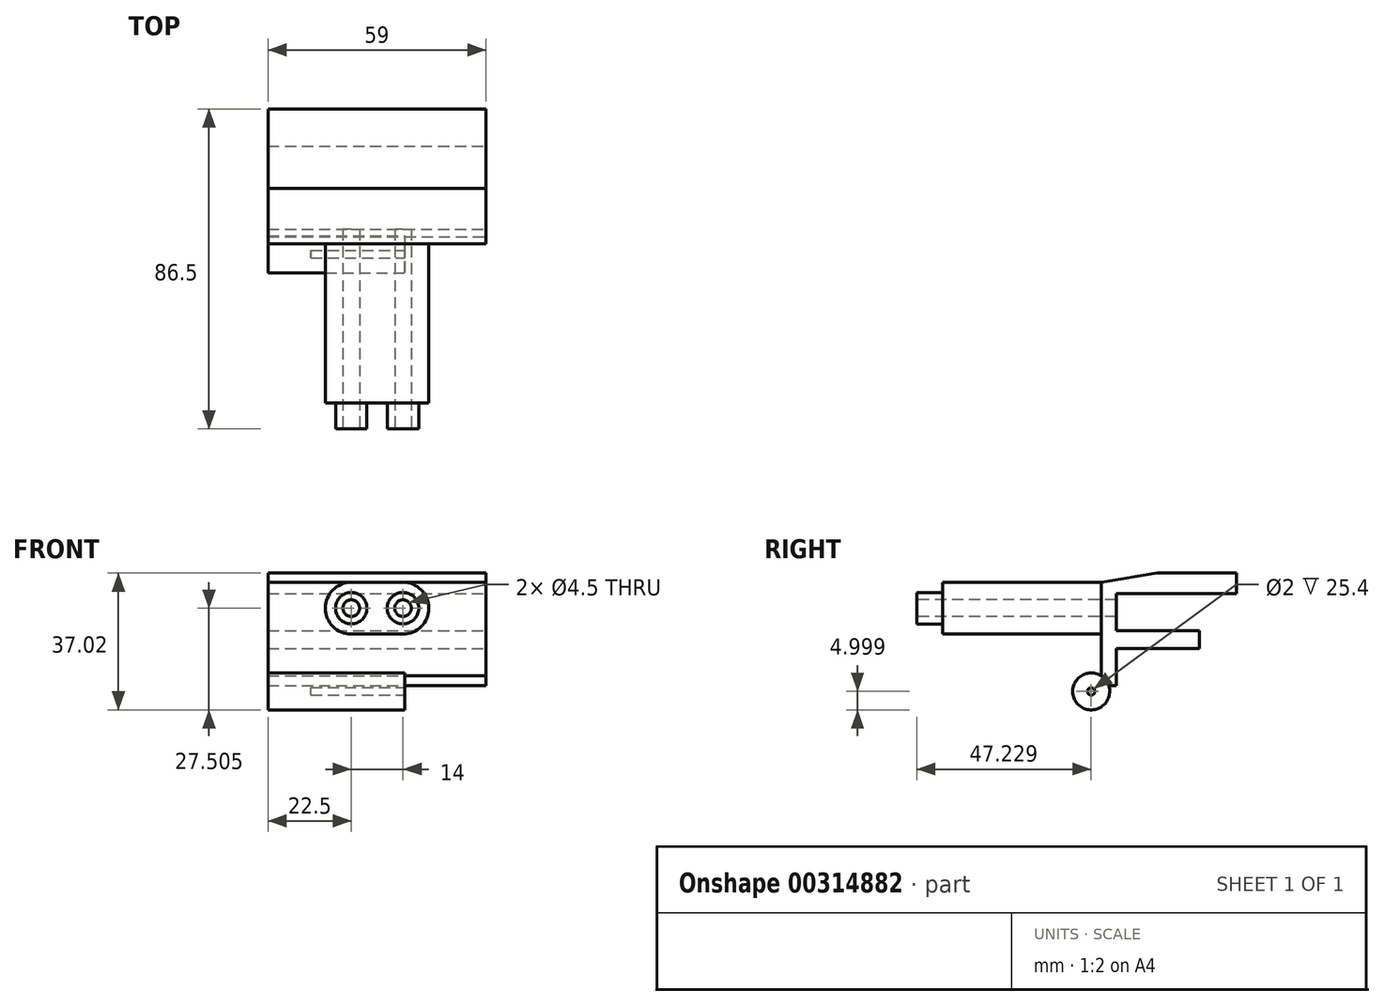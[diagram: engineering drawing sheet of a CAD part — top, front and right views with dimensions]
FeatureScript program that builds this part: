
annotation { "Feature Type Name" : "Feature", "Feature Type Description" : "" }
export const myFeature = defineFeature(function(context is Context, id is Id, definition is map)
    precondition{}
    {
        {
            var Q0;
            Q0=qCreatedBy(makeId("Right.planeOp"),FACE);
            var sketch = newSketch(context, id + "F0", { "sketchPlane" : qUnion([Q0])});
            skLineSegment(sketch, "E0.bottom", {"start": v(-27.18, 24.44) * mm, "end": v(67.82, 24.44) * mm});
            skLineSegment(sketch, "E0.top", {"start": v(-27.18, -25.56) * mm, "end": v(67.82, -25.56) * mm});
            skLineSegment(sketch, "E0.left", {"start": v(-27.18, 24.44) * mm, "end": v(-27.18, -25.56) * mm});
            skLineSegment(sketch, "E0.right", {"start": v(67.82, 24.44) * mm, "end": v(67.82, -25.56) * mm});
            skSolve(sketch);
        }
        {
            var Q0;
            Q0=makeQuery(id+"F0.imprint","IMPRINT",FACE,{"disambiguationData":[TD([[makeQuery(id+"F0.imprint","IMPRINT",EDGE,{"derivedFrom":sQuery(id+"F0.wireOp",EDGE,"E0.bottom")}),-1.0]])]});
            extrude(context, id + "F1", {"entities" : qUnion([Q0]), "endBound" : BoundingType.SYMMETRIC, "depth" : 59 * mm});
        }
        {
            var Q0;
            Q0=makeQuery(id+"F1.opExtrude","CAP_FACE",FACE,{"disambiguationData":[OSD([sQuery(id+"F0.wireOp",EDGE,"E0.bottom"),sQuery(id+"F0.wireOp",EDGE,"E0.top"),sQuery(id+"F0.wireOp",EDGE,"E0.left"),sQuery(id+"F0.wireOp",EDGE,"E0.right")])],"isStart":false});
            var sketch = newSketch(context, id + "F2", { "sketchPlane" : qUnion([Q0])});
            skLineSegment(sketch, "E1", {"start": v(-21.45, 24.44) * mm, "end": v(-21.45, 18.29) * mm});
            skLineSegment(sketch, "E2", {"start": v(-21.45, 18.29) * mm, "end": v(-13.49, 18.29) * mm});
            skLineSegment(sketch, "E3", {"start": v(-13.49, 18.29) * mm, "end": v(-21.45, 24.44) * mm});
            skLineSegment(sketch, "E4", {"start": v(-21.45, 18.29) * mm, "end": v(-27.18, 18.29) * mm});
            skLineSegment(sketch, "E5", {"start": v(-27.18, 18.29) * mm, "end": v(-27.18, 4.29) * mm});
            skLineSegment(sketch, "E6", {"start": v(-27.18, 4.29) * mm, "end": v(22.82, 4.29) * mm});
            skLineSegment(sketch, "E7", {"start": v(-27.18, 11.29) * mm, "end": v(26.82, 11.29) * mm});
            skLineSegment(sketch, "E8", {"start": v(-13.49, 18.29) * mm, "end": v(22.82, 18.29) * mm});
            skPoint(sketch, "E9.endSnap0", {"position": v(21.6, 18.29) * mm});
            skLineSegment(sketch, "E10", {"start": v(22.82, 18.29) * mm, "end": v(37.83, 20.8) * mm});
            skLineSegment(sketch, "E11", {"start": v(22.82, 4.29) * mm, "end": v(22.82, -9.71) * mm});
            skLineSegment(sketch, "E12", {"start": v(22.82, -9.71) * mm, "end": v(26.82, -9.71) * mm});
            skLineSegment(sketch, "E13", {"start": v(26.82, -9.71) * mm, "end": v(26.82, 15.29) * mm});
            skArc(sketch, "E14", {"start": v(22.82, -7.06) * mm, "mid": v(16.05, -14.23) * mm, "end": v(24.82, -9.71) * mm});
            skPoint(sketch, "E15.end.orphan", {"position": v(34.19, -8.71) * mm});
            skLineSegment(sketch, "E16", {"start": v(26.82, 5.19) * mm, "end": v(49.32, 5.19) * mm});
            skLineSegment(sketch, "E17", {"start": v(49.32, 5.19) * mm, "end": v(49.32, 0.39) * mm});
            skLineSegment(sketch, "E18", {"start": v(49.32, 0.39) * mm, "end": v(26.82, 0.39) * mm});
            skLineSegment(sketch, "E19", {"start": v(26.82, 15.29) * mm, "end": v(59.32, 15.29) * mm});
            skLineSegment(sketch, "E20", {"start": v(37.83, 20.8) * mm, "end": v(59.32, 20.8) * mm});
            skLineSegment(sketch, "E21", {"start": v(59.32, 20.8) * mm, "end": v(59.32, 15.29) * mm});
            skSolve(sketch);
        }
        {
            var Q0;
            {var subQ0=sQuery(id+"F2.wireOp",EDGE,"E1");Q0=makeQuery(id+"F2.imprint","IMPRINT",FACE,{"disambiguationData":[TD([[makeQuery(id+"F2.imprint","IMPRINT",EDGE,{"derivedFrom":subQ0}),-1.0]])]});}
            var Q1;
            {var subQ9=sQuery(id+"F2.wireOp",EDGE,"E3");Q1=makeQuery(id+"F2.imprint","IMPRINT",FACE,{"disambiguationData":[TD([[makeQuery(id+"F2.imprint","IMPRINT",EDGE,{"derivedFrom":subQ9}),-1.0]])]});}
            extrude(context, id + "F3", {"entities" : qUnion([Q0, Q1]), "operationType" : NewBodyOperationType.REMOVE, "endBound" : BoundingType.THROUGH_ALL, "oppositeDirection" : true, "depth" : 25.4 * mm});
        }
        {
            var Q0;
            Q0=makeQuery(id+"F1.opExtrude","CAP_FACE",FACE,{"disambiguationData":[OSD([sQuery(id+"F0.wireOp",EDGE,"E0.bottom"),sQuery(id+"F0.wireOp",EDGE,"E0.top"),sQuery(id+"F0.wireOp",EDGE,"E0.left"),sQuery(id+"F0.wireOp",EDGE,"E0.right")])],"isStart":false});
            var sketch = newSketch(context, id + "F4", { "sketchPlane" : qUnion([Q0])});
            skCircle(sketch, "E22", {"center": v(20.05, -11.22) * mm, "radius": 5 * mm});
            skSolve(sketch);
        }
        {
            var Q0;
            Q0 = qSketchRegion(id + "F4", true);
            extrude(context, id + "F5", {"entities" : qUnion([Q0]), "operationType" : NewBodyOperationType.REMOVE, "oppositeDirection" : true, "depth" : 22 * mm});
        }
        {
            var Q0;
            Q0=makeQuery(id+"F5.boolean.opBoolean","COPY",FACE,{"derivedFrom":makeQuery(id+"F5.opExtrude","CAP_FACE",FACE,{"disambiguationData":[OSD([sQuery(id+"F4.wireOp",EDGE,"E22")])],"isStart":false})});
            var sketch = newSketch(context, id + "F6", { "sketchPlane" : qUnion([Q0])});
            skCircle(sketch, "E23", {"center": v(20.05, -11.22) * mm, "radius": 1 * mm});
            skSolve(sketch);
        }
        {
            var Q0;
            Q0=makeQuery(id+"F6.imprint","IMPRINT",FACE,{"disambiguationData":[TD([[makeQuery(id+"F6.imprint","IMPRINT",EDGE,{"derivedFrom":sQuery(id+"F6.wireOp",EDGE,"E23")}),1.0]])]});
            extrude(context, id + "F7", {"entities" : qUnion([Q0]), "operationType" : NewBodyOperationType.REMOVE, "oppositeDirection" : true, "depth" : 25.4 * mm});
        }
        {
            var Q0;
            Q0=makeQuery(id+"F1.opExtrude","SWEPT_FACE",FACE,{"disambiguationData":[OSD([sQuery(id+"F0.wireOp",EDGE,"E0.left")])]});
            var sketch = newSketch(context, id + "F8", { "sketchPlane" : qUnion([Q0])});
            skArc(sketch, "E24", {"start": v(-7, 18.29) * mm, "mid": v(-14, 11.29) * mm, "end": v(-7, 4.29) * mm});
            skPoint(sketch, "E24.centerSnap0", {"position": v(-29.5, 11.29) * mm});
            skArc(sketch, "E25", {"start": v(7, 4.29) * mm, "mid": v(14, 11.29) * mm, "end": v(7, 18.29) * mm});
            skPoint(sketch, "E25.centerSnap0", {"position": v(29.5, 11.29) * mm});
            skCircle(sketch, "E26", {"center": v(-7, 11.29) * mm, "radius": 2.25 * mm});
            skCircle(sketch, "E27", {"center": v(7, 11.29) * mm, "radius": 2.25 * mm});
            skLineSegment(sketch, "E28", {"start": v(-7, 18.29) * mm, "end": v(7, 18.29) * mm});
            skLineSegment(sketch, "E29", {"start": v(-7, 4.29) * mm, "end": v(7, 4.29) * mm});
            skPoint(sketch, "E30.end.orphan", {"position": v(0, 4.29) * mm});
            skPoint(sketch, "E30.start.orphan", {"position": v(0, 18.29) * mm});
            skSolve(sketch);
        }
        {
            var Q0;
            {var subQ0=sQuery(id+"F8.wireOp",EDGE,"E25");Q0=makeQuery(id+"F8.imprint","IMPRINT",FACE,{"disambiguationData":[TD([[makeQuery(id+"F8.imprint","IMPRINT",EDGE,{"derivedFrom":subQ0}),-1.0]])]});}
            var Q1;
            {var subQ0=sQuery(id+"F8.wireOp",EDGE,"E24");Q1=makeQuery(id+"F8.imprint","IMPRINT",FACE,{"disambiguationData":[TD([[makeQuery(id+"F8.imprint","IMPRINT",EDGE,{"derivedFrom":subQ0}),-1.0]])]});}
            var Q2;
            Q2=makeQuery(id+"F8.imprint","IMPRINT",FACE,{"disambiguationData":[TD([[makeQuery(id+"F8.imprint","IMPRINT",EDGE,{"derivedFrom":sQuery(id+"F8.wireOp",EDGE,"E26")}),1.0]])]});
            var Q3;
            Q3=makeQuery(id+"F8.imprint","IMPRINT",FACE,{"disambiguationData":[TD([[makeQuery(id+"F8.imprint","IMPRINT",EDGE,{"derivedFrom":sQuery(id+"F8.wireOp",EDGE,"E27")}),1.0]])]});
            extrude(context, id + "F9", {"entities" : qUnion([Q0, Q1, Q2, Q3]), "operationType" : NewBodyOperationType.REMOVE, "oppositeDirection" : true, "depth" : 50 * mm});
        }
        {
            var Q0;
            Q0=makeQuery(id+"F9.boolean.opBoolean","COPY",FACE,{"derivedFrom":makeQuery(id+"F9.opExtrude","CAP_FACE",FACE,{"disambiguationData":[OSD([sQuery(id+"F8.wireOp",EDGE,"E26")])],"isStart":false})});
            var Q1;
            Q1=makeQuery(id+"F9.boolean.opBoolean","COPY",FACE,{"derivedFrom":makeQuery(id+"F9.opExtrude","CAP_FACE",FACE,{"disambiguationData":[OSD([sQuery(id+"F8.wireOp",EDGE,"E27")])],"isStart":false})});
            extrude(context, id + "F10", {"entities" : qUnion([Q0, Q1]), "operationType" : NewBodyOperationType.REMOVE, "endBound" : BoundingType.THROUGH_ALL, "oppositeDirection" : true, "depth" : 25 * mm});
        }
        {
            var Q0;
            Q0=makeQuery(id+"F3.boolean.opBoolean","COPY",FACE,{"derivedFrom":makeQuery(id+"F3.opExtrude","SWEPT_FACE",FACE,{"disambiguationData":[OSD([sQuery(id+"F2.wireOp",EDGE,"E1")])]})});
            var sketch = newSketch(context, id + "F11", { "sketchPlane" : qUnion([Q0])});
            skLineSegment(sketch, "E31", {"start": v(-7, 18.29) * mm, "end": v(-7, 24.44) * mm});
            skLineSegment(sketch, "E32", {"start": v(7, 18.29) * mm, "end": v(7, 24.44) * mm});
            skSolve(sketch);
        }
        {
            var Q0;
            Q0 = qSketchRegion(id + "F11", true);
            var Q1;
            {var subQ0=sQuery(id+"F11.wireOp",EDGE,"E31");Q1=makeQuery(id+"F11.imprint","IMPRINT",FACE,{"disambiguationData":[TD([[makeQuery(id+"F11.imprint","IMPRINT",EDGE,{"derivedFrom":subQ0}),1.0]])]});}
            var Q2;
            {var subQ0=sQuery(id+"F11.wireOp",EDGE,"E32");Q2=makeQuery(id+"F11.imprint","IMPRINT",FACE,{"disambiguationData":[TD([[makeQuery(id+"F11.imprint","IMPRINT",EDGE,{"derivedFrom":subQ0}),-1.0]])]});}
            extrude(context, id + "F12", {"entities" : qUnion([Q0, Q1, Q2]), "operationType" : NewBodyOperationType.REMOVE, "oppositeDirection" : true, "depth" : 25 * mm});
        }
        {
            var Q0;
            Q0=makeQuery(id+"F12.boolean.opBoolean","COPY",FACE,{"derivedFrom":makeQuery(id+"F12.opExtrude","SWEPT_FACE",FACE,{"disambiguationData":[OSD([sQuery(id+"F11.wireOp",EDGE,"E31")])]})});
            extrude(context, id + "F13", {"entities" : qUnion([Q0]), "operationType" : NewBodyOperationType.REMOVE, "oppositeDirection" : true, "depth" : 5 * mm});
        }
        {
            var Q0;
            Q0=makeQuery(id+"F12.boolean.opBoolean","COPY",FACE,{"derivedFrom":makeQuery(id+"F12.opExtrude","SWEPT_FACE",FACE,{"disambiguationData":[OSD([sQuery(id+"F11.wireOp",EDGE,"E32")])]})});
            extrude(context, id + "F14", {"entities" : qUnion([Q0]), "operationType" : NewBodyOperationType.REMOVE, "oppositeDirection" : true, "depth" : 5 * mm});
        }
        {
            var Q0;
            Q0=makeQuery(id+"F13.boolean.opBoolean","COPY",FACE,{"derivedFrom":makeQuery(id+"F13.opExtrude","CAP_FACE",FACE,{"disambiguationData":[OSD([sQuery(id+"F11.wireOp",EDGE,"E31")])],"isStart":false})});
            var sketch = newSketch(context, id + "F15", { "sketchPlane" : qUnion([Q0])});
            skFitSpline(sketch, "E33", {"points": [v(21.45, 24.44) * mm, v(19.48, 20.4) * mm, v(13.49, 18.29) * mm], "startDerivative": vector(0, -5.6) * mm, "endDerivative": vector(-11.26, 0) * mm});
            skSolve(sketch);
        }
        {
            var Q0;
            Q0=makeQuery(id+"F15.imprint","IMPRINT",FACE,{"disambiguationData":[TD([[makeQuery(id+"F15.imprint","IMPRINT",EDGE,{"derivedFrom":sQuery(id+"F15.wireOp",EDGE,"E33")}),-1.0]])]});
            extrude(context, id + "F16", {"entities" : qUnion([Q0]), "operationType" : NewBodyOperationType.REMOVE, "oppositeDirection" : true, "depth" : 25 * mm});
        }
        {
            var Q0;
            Q0=makeQuery(id+"F3.boolean.opBoolean","COPY",FACE,{"derivedFrom":makeQuery(id+"F3.opExtrude","SWEPT_FACE",FACE,{"disambiguationData":[OSD([sQuery(id+"F2.wireOp",EDGE,"E1")])]})});
            var sketch = newSketch(context, id + "F17", { "sketchPlane" : qUnion([Q0])});
            skLineSegment(sketch, "E34.bottom", {"start": v(-0.5, 24.44) * mm, "end": v(0.5, 24.44) * mm});
            skLineSegment(sketch, "E34.top", {"start": v(-0.5, 20.04) * mm, "end": v(0.5, 20.04) * mm});
            skLineSegment(sketch, "E34.left", {"start": v(0.5, 24.44) * mm, "end": v(0.5, 20.04) * mm});
            skLineSegment(sketch, "E34.right", {"start": v(-0.5, 24.44) * mm, "end": v(-0.5, 20.04) * mm});
            skLineSegment(sketch, "E35.bottom", {"start": v(-0.5, 20.04) * mm, "end": v(-2, 20.04) * mm});
            skLineSegment(sketch, "E35.top", {"start": v(-0.5, 24.44) * mm, "end": v(-2, 24.44) * mm});
            skLineSegment(sketch, "E35.left", {"start": v(-0.5, 20.04) * mm, "end": v(-0.5, 24.44) * mm});
            skLineSegment(sketch, "E35.right", {"start": v(-2, 20.04) * mm, "end": v(-2, 24.44) * mm});
            skLineSegment(sketch, "E36.bottom", {"start": v(0.5, 20.04) * mm, "end": v(2, 20.04) * mm});
            skLineSegment(sketch, "E36.top", {"start": v(0.5, 24.44) * mm, "end": v(2, 24.44) * mm});
            skLineSegment(sketch, "E36.left", {"start": v(0.5, 20.04) * mm, "end": v(0.5, 24.44) * mm});
            skLineSegment(sketch, "E36.right", {"start": v(2, 20.04) * mm, "end": v(2, 24.44) * mm});
            skSolve(sketch);
        }
        {
            var Q0;
            Q0=makeQuery(id+"F17.imprint","IMPRINT",FACE,{"disambiguationData":[TD([[makeQuery(id+"F17.imprint","IMPRINT",EDGE,{"derivedFrom":sQuery(id+"F17.wireOp",EDGE,"E35.bottom")}),-1.0]])]});
            var Q1;
            Q1=makeQuery(id+"F17.imprint","IMPRINT",FACE,{"disambiguationData":[TD([[makeQuery(id+"F17.imprint","IMPRINT",EDGE,{"derivedFrom":sQuery(id+"F17.wireOp",EDGE,"E36.bottom")}),1.0]])]});
            extrude(context, id + "F18", {"entities" : qUnion([Q0, Q1]), "operationType" : NewBodyOperationType.REMOVE, "oppositeDirection" : true, "depth" : 25 * mm});
        }
        {
            var Q0;
            Q0=makeQuery(id+"F3.boolean.opBoolean","COPY",FACE,{"derivedFrom":makeQuery(id+"F3.opExtrude","SWEPT_FACE",FACE,{"disambiguationData":[OSD([sQuery(id+"F2.wireOp",EDGE,"E1")])]})});
            var sketch = newSketch(context, id + "F19", { "sketchPlane" : qUnion([Q0])});
            skLineSegment(sketch, "E37.bottom", {"start": v(-0.5, 24.44) * mm, "end": v(0.5, 24.44) * mm});
            skLineSegment(sketch, "E37.top", {"start": v(-0.5, 22.85) * mm, "end": v(0.5, 22.85) * mm});
            skLineSegment(sketch, "E37.left", {"start": v(-0.5, 24.44) * mm, "end": v(-0.5, 22.85) * mm});
            skLineSegment(sketch, "E37.right", {"start": v(0.5, 24.44) * mm, "end": v(0.5, 22.85) * mm});
            skSolve(sketch);
        }
        {
            var Q0;
            Q0=makeQuery(id+"F19.imprint","IMPRINT",FACE,{"disambiguationData":[TD([[makeQuery(id+"F19.imprint","IMPRINT",EDGE,{"derivedFrom":sQuery(id+"F19.wireOp",EDGE,"E37.bottom")}),-1.0]])]});
            extrude(context, id + "F20", {"entities" : qUnion([Q0]), "operationType" : NewBodyOperationType.REMOVE, "oppositeDirection" : true, "depth" : 25 * mm});
        }
        {
            var Q0;
            Q0=makeQuery(id+"F1.opExtrude","SWEPT_FACE",FACE,{"disambiguationData":[OSD([sQuery(id+"F0.wireOp",EDGE,"E0.left")])]});
            var sketch = newSketch(context, id + "F21", { "sketchPlane" : qUnion([Q0])});
            skCircle(sketch, "E38", {"center": v(-7, 11.29) * mm, "radius": 4.25 * mm});
            skCircle(sketch, "E39", {"center": v(7, 11.29) * mm, "radius": 4.25 * mm});
            skSolve(sketch);
        }
        {
            var Q0;
            Q0=makeQuery(id+"F21.imprint","IMPRINT",FACE,{"disambiguationData":[TD([[makeQuery(id+"F21.imprint","IMPRINT",EDGE,{"derivedFrom":sQuery(id+"F21.wireOp",EDGE,"E38")}),-1.0]])]});
            extrude(context, id + "F22", {"entities" : qUnion([Q0]), "operationType" : NewBodyOperationType.REMOVE, "oppositeDirection" : true, "depth" : 7 * mm});
        }
        {
            var Q0;
            Q0=makeQuery(id+"F14.boolean.opBoolean","COPY",FACE,{"derivedFrom":makeQuery(id+"F14.opExtrude","CAP_FACE",FACE,{"disambiguationData":[OSD([sQuery(id+"F11.wireOp",EDGE,"E32")])],"isStart":false})});
            var sketch = newSketch(context, id + "F23", { "sketchPlane" : qUnion([Q0])});
            skLineSegment(sketch, "E40.bottom", {"start": v(-21.45, 18.29) * mm, "end": v(-5.78, 18.29) * mm});
            skLineSegment(sketch, "E40.top", {"start": v(-21.45, 25.74) * mm, "end": v(-5.78, 25.74) * mm});
            skLineSegment(sketch, "E40.left", {"start": v(-21.45, 18.29) * mm, "end": v(-21.45, 25.74) * mm});
            skLineSegment(sketch, "E40.right", {"start": v(-5.78, 18.29) * mm, "end": v(-5.78, 25.74) * mm});
            skSolve(sketch);
        }
        {
            var Q0;
            Q0 = qSketchRegion(id + "F23", true);
            extrude(context, id + "F24", {"entities" : qUnion([Q0]), "operationType" : NewBodyOperationType.REMOVE, "oppositeDirection" : true, "depth" : 25 * mm});
        }
    });
